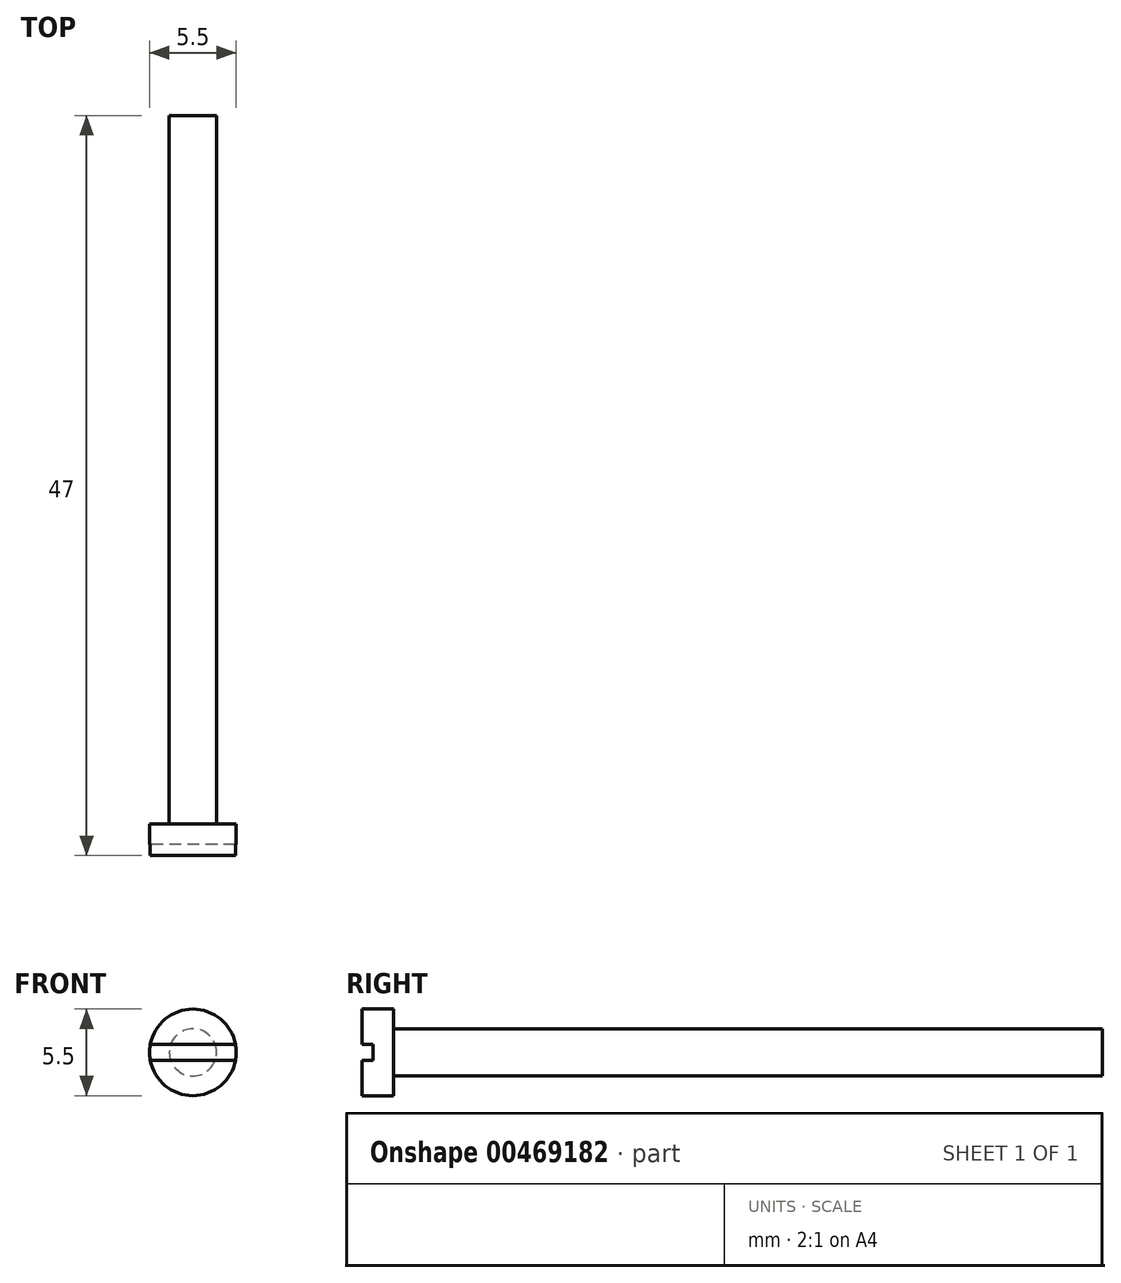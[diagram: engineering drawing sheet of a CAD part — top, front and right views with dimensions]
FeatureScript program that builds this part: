
annotation { "Feature Type Name" : "Feature", "Feature Type Description" : "" }
export const myFeature = defineFeature(function(context is Context, id is Id, definition is map)
    precondition{}
    {
        {
            var Q0;
            Q0=qCreatedBy(makeId("Front.planeOp"),FACE);
            var sketch = newSketch(context, id + "F0", { "sketchPlane" : qUnion([Q0])});
            skCircle(sketch, "E0", {"center": v(0, 0) * mm, "radius": 2.75 * mm});
            skSolve(sketch);
        }
        {
            var Q0;
            Q0=makeQuery(id+"F0.imprint","IMPRINT",FACE,{"disambiguationData":[TD([[makeQuery(id+"F0.imprint","IMPRINT",EDGE,{"derivedFrom":sQuery(id+"F0.wireOp",EDGE,"E0")}),1.0]])]});
            extrude(context, id + "F1", {"entities" : qUnion([Q0]), "depth" : 2 * mm});
        }
        {
            var Q0;
            Q0=makeQuery(id+"F1.opExtrude","CAP_FACE",FACE,{"disambiguationData":[OSD([sQuery(id+"F0.wireOp",EDGE,"E0")])],"isStart":false});
            var sketch = newSketch(context, id + "F2", { "sketchPlane" : qUnion([Q0])});
            skLineSegment(sketch, "E1.bottom", {"start": v(3.08, 0.5) * mm, "end": v(-3.08, 0.5) * mm});
            skLineSegment(sketch, "E1.top", {"start": v(3.08, -0.5) * mm, "end": v(-3.08, -0.5) * mm});
            skLineSegment(sketch, "E1.left", {"start": v(3.08, 0.5) * mm, "end": v(3.08, -0.5) * mm});
            skLineSegment(sketch, "E1.right", {"start": v(-3.08, 0.5) * mm, "end": v(-3.08, -0.5) * mm});
            skPoint(sketch, "E1.middle", {"position": v(0, 0) * mm});
            skSolve(sketch);
        }
        {
            var Q0;
            {var subQ0=sQuery(id+"F2.wireOp",EDGE,"E1.bottom");var subQ1=makeQuery(id+"F1.opExtrude","CAP_EDGE",EDGE,{"disambiguationData":[OSD([sQuery(id+"F0.wireOp",EDGE,"E0")])],"isStart":false});var subQ2=makeQuery(id+"F2.imprint","INTERSECT",VERTEX,{"disambiguationData":[OD(0.0)],"derivedFrom":[subQ1,subQ0]});Q0=makeQuery(id+"F2.imprint","IMPRINT",FACE,{"disambiguationData":[TD([[makeQuery(id+"F2.imprint","IMPRINT",EDGE,{"disambiguationData":[TD([[subQ2,-1.0]])],"derivedFrom":subQ0}),1.0]])]});}
            extrude(context, id + "F3", {"entities" : qUnion([Q0]), "operationType" : NewBodyOperationType.REMOVE, "oppositeDirection" : true, "depth" : 0.7 * mm});
        }
        {
            var Q0;
            Q0=makeQuery(id+"F1.opExtrude","CAP_FACE",FACE,{"disambiguationData":[OSD([sQuery(id+"F0.wireOp",EDGE,"E0")])],"isStart":true});
            var sketch = newSketch(context, id + "F4", { "sketchPlane" : qUnion([Q0])});
            skCircle(sketch, "E2", {"center": v(0, 0) * mm, "radius": 1.5 * mm});
            skSolve(sketch);
        }
        {
            var Q0;
            Q0=makeQuery(id+"F4.imprint","IMPRINT",FACE,{"disambiguationData":[TD([[makeQuery(id+"F4.imprint","IMPRINT",EDGE,{"derivedFrom":sQuery(id+"F4.wireOp",EDGE,"E2")}),1.0]])]});
            extrude(context, id + "F5", {"entities" : qUnion([Q0]), "operationType" : NewBodyOperationType.ADD, "depth" : 45 * mm});
        }
    });
